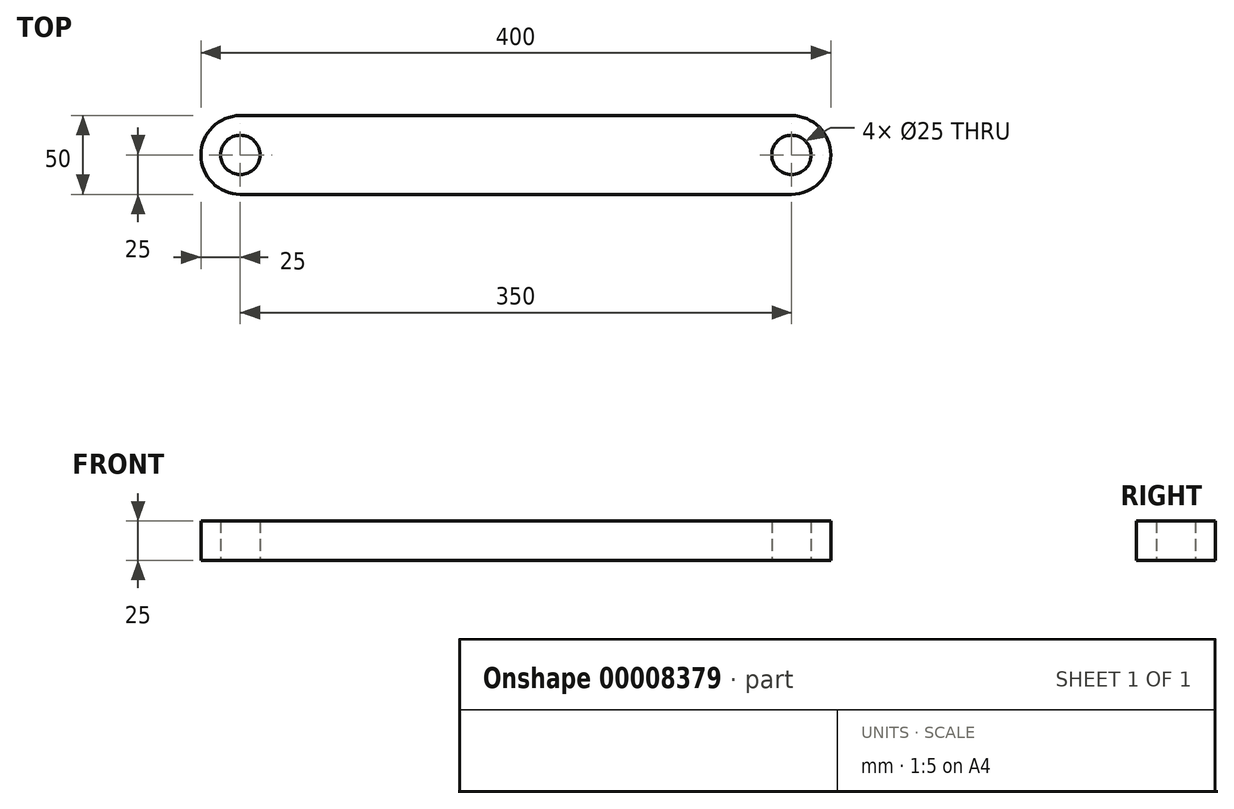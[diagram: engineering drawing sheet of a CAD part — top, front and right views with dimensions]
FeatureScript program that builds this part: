
annotation { "Feature Type Name" : "Feature", "Feature Type Description" : "" }
export const myFeature = defineFeature(function(context is Context, id is Id, definition is map)
    precondition{}
    {
        {
            var Q0;
            Q0=qCreatedBy(makeId("Top.planeOp"),FACE);
            var sketch = newSketch(context, id + "F0", { "sketchPlane" : qUnion([Q0])});
            skLineSegment(sketch, "E0.rect.bottom", {"start": v(175, 25) * mm, "end": v(-175, 25) * mm});
            skLineSegment(sketch, "E0.rect.top", {"start": v(175, -25) * mm, "end": v(-175, -25) * mm});
            skPoint(sketch, "E0.rect.middle", {"position": v(0, 0) * mm});
            skArc(sketch, "E1", {"start": v(-175, 25) * mm, "mid": v(-200, 0) * mm, "end": v(-175, -25) * mm});
            skCircle(sketch, "E2", {"center": v(-175, 0) * mm, "radius": 12.5 * mm});
            skArc(sketch, "E3", {"start": v(175, -25) * mm, "mid": v(200, 0) * mm, "end": v(175, 25) * mm});
            skCircle(sketch, "E4", {"center": v(175, 0) * mm, "radius": 12.5 * mm});
            skSolve(sketch);
        }
        {
            var Q0;
            Q0 = qSketchRegion(id + "F0", true);
            extrude(context, id + "F1", {"entities" : qUnion([Q0]), "depth" : 25 * mm});
        }
    });
